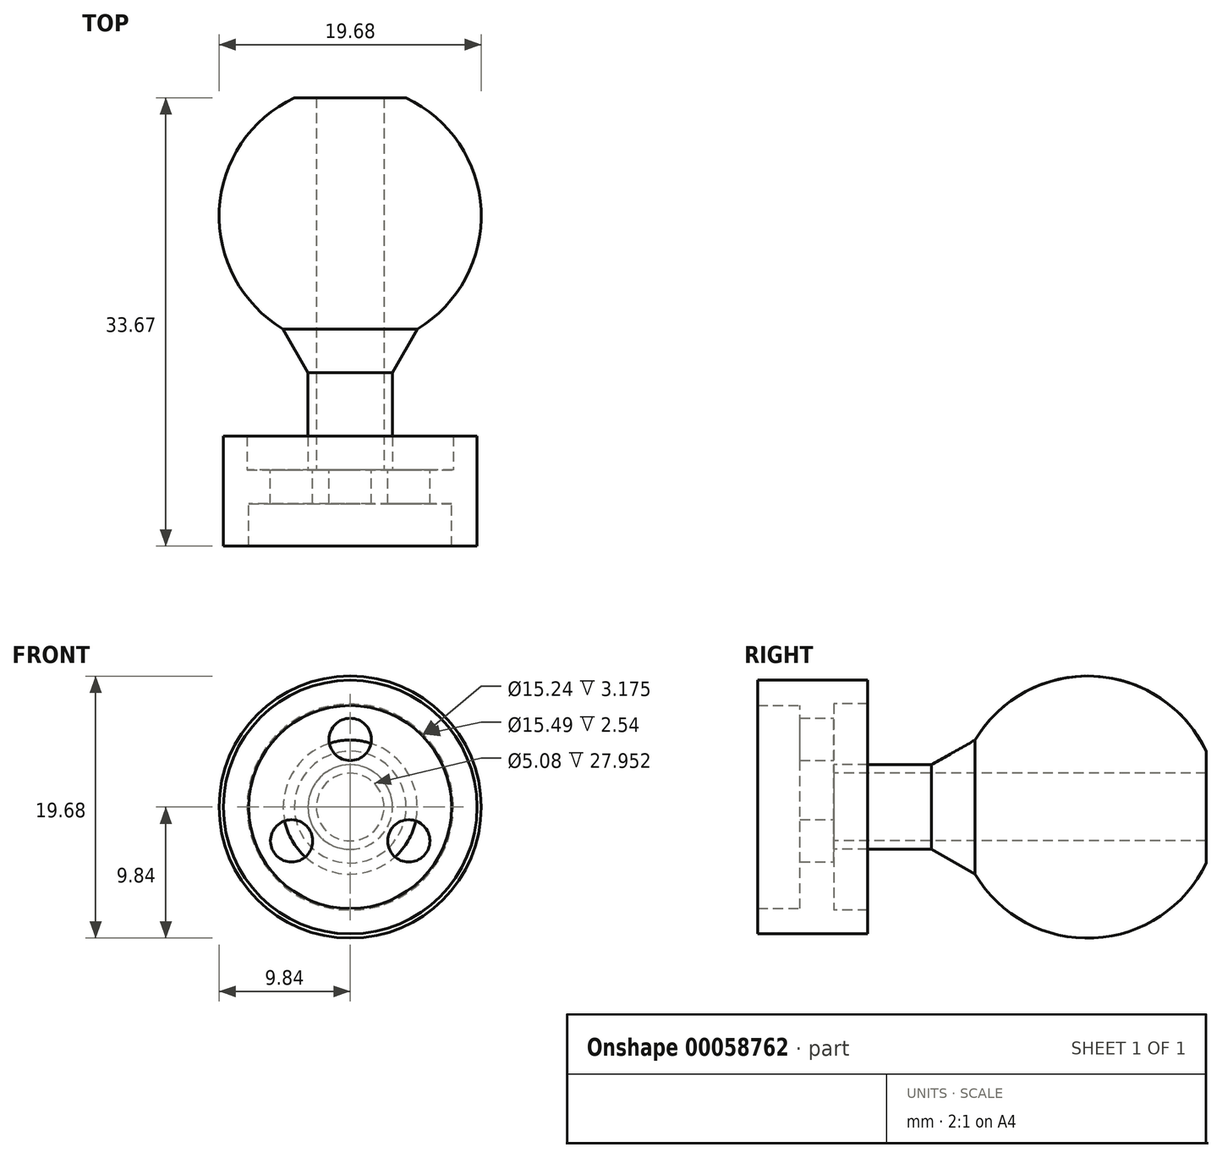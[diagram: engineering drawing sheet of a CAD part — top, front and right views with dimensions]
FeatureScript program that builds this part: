
annotation { "Feature Type Name" : "Feature", "Feature Type Description" : "" }
export const myFeature = defineFeature(function(context is Context, id is Id, definition is map)
    precondition{}
    {
        {
            var Q0;
            Q0=qCreatedBy(makeId("Front.planeOp"),FACE);
            var sketch = newSketch(context, id + "F0", { "sketchPlane" : qUnion([Q0])});
            skCircle(sketch, "E0", {"center": v(0, 0) * mm, "radius": 9.53 * mm});
            skCircle(sketch, "E1", {"center": v(0, 0) * mm, "radius": 5.08 * mm, "construction": true});
            skCircle(sketch, "E2", {"center": v(0, 5.08) * mm, "radius": 1.59 * mm});
            skCircle(sketch, "E3.1.0", {"center": v(-4.4, -2.54) * mm, "radius": 1.59 * mm});
            skCircle(sketch, "E3.2.0", {"center": v(4.4, -2.54) * mm, "radius": 1.59 * mm});
            skSolve(sketch);
        }
        {
            var Q0;
            Q0 = qSketchRegion(id + "F0", true);
            extrude(context, id + "F1", {"entities" : qUnion([Q0]), "depth" : 2.54 * mm});
        }
        {
            var Q0;
            Q0=makeQuery(id+"F1.opExtrude","CAP_FACE",FACE,{"disambiguationData":[OSD([sQuery(id+"F0.wireOp",EDGE,"E0"),sQuery(id+"F0.wireOp",EDGE,"E2"),sQuery(id+"F0.wireOp",EDGE,"E3.1.0"),sQuery(id+"F0.wireOp",EDGE,"E3.2.0")])],"isStart":false});
            var sketch = newSketch(context, id + "F2", { "sketchPlane" : qUnion([Q0])});
            skCircle(sketch, "E4", {"center": v(0, 0) * mm, "radius": 9.53 * mm});
            skCircle(sketch, "E5", {"center": v(0, 0) * mm, "radius": 7.62 * mm});
            skSolve(sketch);
        }
        {
            var Q0;
            Q0 = qSketchRegion(id + "F2", true);
            extrude(context, id + "F3", {"entities" : qUnion([Q0]), "operationType" : NewBodyOperationType.ADD, "depth" : 3.17 * mm});
        }
        {
            var Q0;
            Q0=makeQuery(id+"F1.opExtrude","CAP_FACE",FACE,{"disambiguationData":[OSD([sQuery(id+"F0.wireOp",EDGE,"E0"),sQuery(id+"F0.wireOp",EDGE,"E2"),sQuery(id+"F0.wireOp",EDGE,"E3.1.0"),sQuery(id+"F0.wireOp",EDGE,"E3.2.0")])],"isStart":true});
            var sketch = newSketch(context, id + "F4", { "sketchPlane" : qUnion([Q0])});
            skCircle(sketch, "E6", {"center": v(0, 0) * mm, "radius": 3.17 * mm});
            skCircle(sketch, "E7", {"center": v(0, 0) * mm, "radius": 9.53 * mm});
            skCircle(sketch, "E8", {"center": v(0, 0) * mm, "radius": 7.75 * mm});
            skSolve(sketch);
        }
        {
            var Q0;
            Q0 = qSketchRegion(id + "F4", true);
            extrude(context, id + "F5", {"entities" : qUnion([Q0]), "operationType" : NewBodyOperationType.ADD, "depth" : 2.54 * mm});
        }
        {
            var Q0;
            Q0=makeQuery(id+"F1.opExtrude","CAP_FACE",FACE,{"disambiguationData":[OSD([sQuery(id+"F0.wireOp",EDGE,"E0"),sQuery(id+"F0.wireOp",EDGE,"E2"),sQuery(id+"F0.wireOp",EDGE,"E3.1.0"),sQuery(id+"F0.wireOp",EDGE,"E3.2.0")])],"isStart":true});
            var sketch = newSketch(context, id + "F6", { "sketchPlane" : qUnion([Q0])});
            skCircle(sketch, "E9", {"center": v(0, 0) * mm, "radius": 3.18 * mm});
            skSolve(sketch);
        }
        {
            var Q0;
            Q0 = qSketchRegion(id + "F6", true);
            extrude(context, id + "F7", {"entities" : qUnion([Q0]), "operationType" : NewBodyOperationType.ADD, "depth" : 12.7 * mm});
        }
        {
            var Q0;
            Q0=qCreatedBy(makeId("Top.planeOp"),FACE);
            var sketch = newSketch(context, id + "F8", { "sketchPlane" : qUnion([Q0])});
            skArc(sketch, "E10", {"start": v(0, 9.2) * mm, "mid": v(9.6, 16.9) * mm, "end": v(4.2, 27.95) * mm});
            skLineSegment(sketch, "E11", {"start": v(4.2, 27.95) * mm, "end": v(0, 27.95) * mm});
            skPoint(sketch, "E12", {"position": v(-4.2, 27.95) * mm});
            skPoint(sketch, "E13", {"position": v(4.2, 27.95) * mm});
            skLineSegment(sketch, "E14", {"start": v(0, 32.9) * mm, "end": v(0, -7.03) * mm, "construction": true});
            skPoint(sketch, "E15", {"position": v(0, 27.95) * mm});
            skPoint(sketch, "E16", {"position": v(0, 9.2) * mm});
            skLineSegment(sketch, "E17", {"start": v(0, 27.95) * mm, "end": v(0, 9.2) * mm});
            skSolve(sketch);
        }
        {
            var Q0;
            Q0 = qSketchRegion(id + "F8", true);
            var Q1;
            Q1=sQuery(id+"F8.wireOp",EDGE,"E14");
            revolve(context, id + "F9", {"operationType" : NewBodyOperationType.ADD, "entities" : qUnion([Q0]), "axis" : qUnion([Q1]), "revolveType" : RevolveType.FULL});
        }
        {
            var Q0;
            Q0=makeQuery(id+"F1.opExtrude","CAP_FACE",FACE,{"disambiguationData":[OSD([sQuery(id+"F0.wireOp",EDGE,"E0"),sQuery(id+"F0.wireOp",EDGE,"E2"),sQuery(id+"F0.wireOp",EDGE,"E3.1.0"),sQuery(id+"F0.wireOp",EDGE,"E3.2.0")])],"isStart":true});
            var sketch = newSketch(context, id + "F10", { "sketchPlane" : qUnion([Q0])});
            skCircle(sketch, "E18", {"center": v(0, 0) * mm, "radius": 2.54 * mm});
            skSolve(sketch);
        }
        {
            var Q0;
            Q0 = qSketchRegion(id + "F10", true);
            extrude(context, id + "F11", {"entities" : qUnion([Q0]), "operationType" : NewBodyOperationType.REMOVE, "endBound" : BoundingType.THROUGH_ALL, "depth" : 25.4 * mm});
        }
        {
            var Q0;
            Q0=makeQuery(id+"F9.boolean.opBoolean","INTERSECT",EDGE,{"derivedFrom":[makeQuery(id+"F7.opExtrude","SWEPT_FACE",FACE,{"disambiguationData":[OSD([sQuery(id+"F6.wireOp",EDGE,"E9")])]}),makeQuery(id+"F9.opRevolve","SWEPT_FACE",FACE,{"disambiguationData":[OSD([sQuery(id+"F8.wireOp",EDGE,"E10")])]})]});
            chamfer(context, id + "F12", {"entities" : qUnion([Q0]), "width" : 3.8 * mm, "tangentPropagation" : true});
        }
    });
